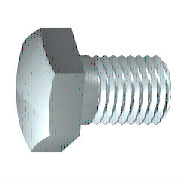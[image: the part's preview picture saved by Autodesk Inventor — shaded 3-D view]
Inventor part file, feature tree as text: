
AUTODESK INVENTOR PART (.ipt)
format: ipt  version: 2025.1 (Build 291241020, 241B)  size: 198,656 bytes
history: native  units: mm (DEFAULTED — no unit token found)
features: extrude x1, chamfer x1, plane x1
ambient origin geometry x7: Origin, YZ Plane, XZ Plane, X Axis, Y Axis, Z Axis, Center Point
bodies: Solid1 (feature_tree), Body (feature_tree)
feature tree (3):
  extrude  "Head"  Depth=25.0mm
  chamfer  "Chamfer1"  Distance=19.7mm
  plane  "Work Plane1"
